# Revit family: Bath_Mixer-GROHE-Allure-32754001
name_source: partatom
category: Plumbing Fixtures
revit_build: Autodesk Revit 2014 (Build: 20130308_1515(x64)
units: mm (PartAtom-declared; Revit-internal decimal feet)

## types (1)
- 32754001
    ADA Compliant = Yes
    Assembly Code = D2020300
    CW Connection = Yes
    CWFU = 3
    Cold Water Connection Diameter = 1/2"
    Default Elevation = 0"
    Description = Allure Single-lever bath mixer 1/2", floor mounted
    Finish = Metal-Grohe-001-Starlight Chrome
    Flow Rate = 7 gpm at 45 psi (26.5 L/min), 2.5 gpm at 80 psi (9.5 L/min) for Hand Shower
    HW Connection = Yes
    HWFU = 3
    Height = 34 5/8"
    Hot Water Connection Diameter = 1"
    Installation Type = Surface Mounted
    Length = 11 7/8"
    Manufacturer = GROHE
    Material = Metal-Grohe-001-Starlight Chrome
    Model = 32754001
    Price = Prices may vary. Please consult Manufacturer Representative for most up-to-date price list.
    Product Page URL = https://www.grohe.us
    Shipping Weight = 29.73 lb
    Tempered Water Connection Diameter = 1/2"
    URL = https://www.grohe.us
    Vent Connection = No
    WFU = 4
    Warranty Information = Limited Lifetime Warranty
    Waste Connection = No
    Width = 6 11/16"

## geometry (parser evidence)
native form markers: Sweep x1
no freeform markers — native parametric forms only
